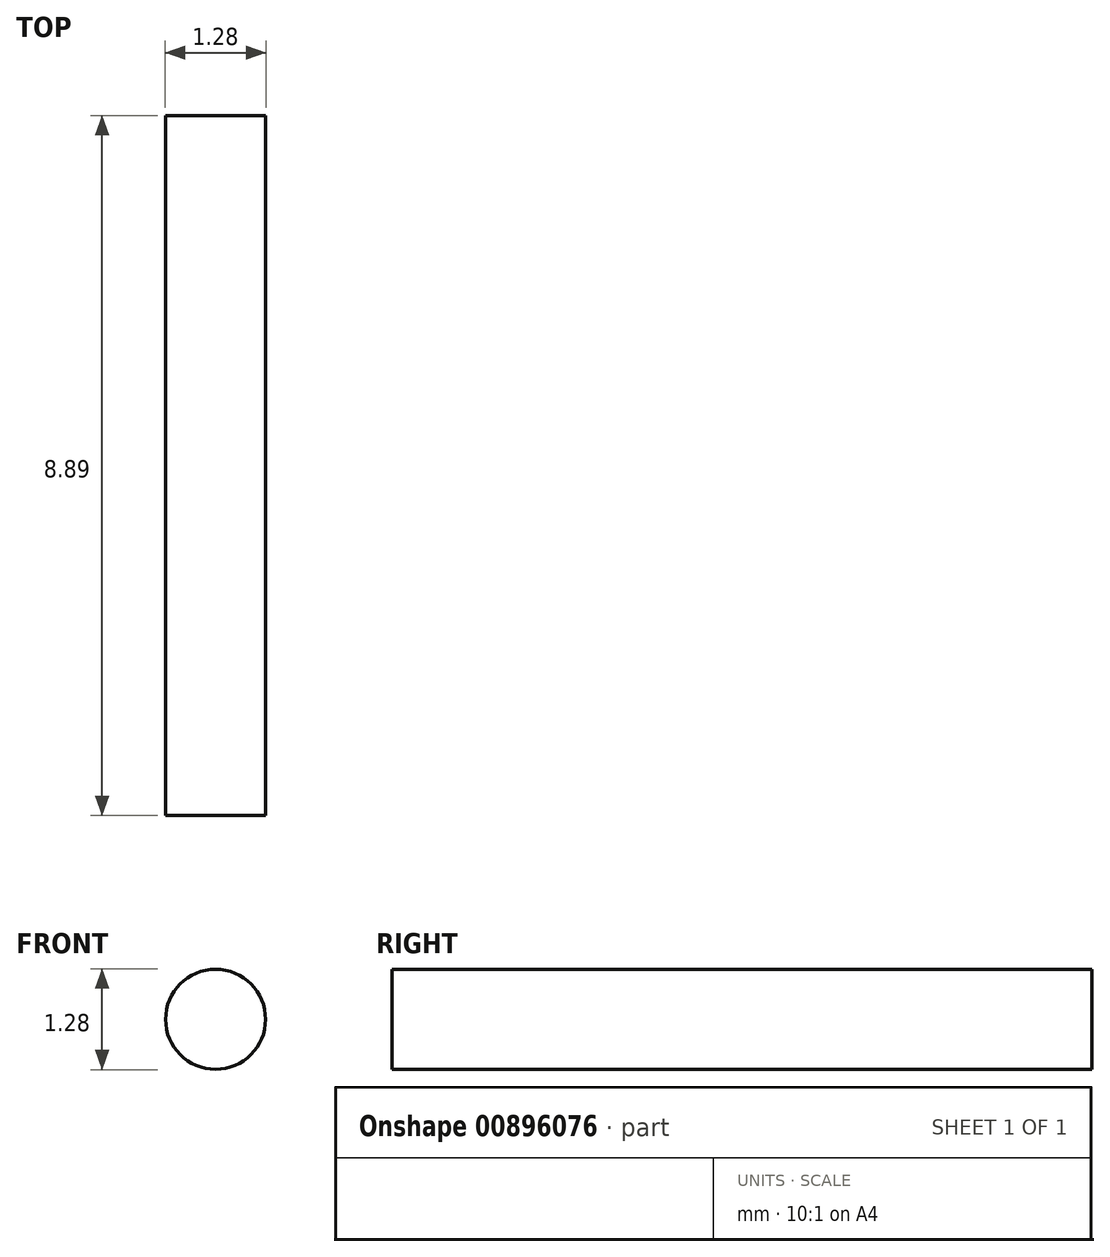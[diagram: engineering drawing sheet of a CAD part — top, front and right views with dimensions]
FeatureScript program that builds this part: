
annotation { "Feature Type Name" : "Feature", "Feature Type Description" : "" }
export const myFeature = defineFeature(function(context is Context, id is Id, definition is map)
    precondition{}
    {
        {
            var Q0;
            Q0=qCreatedBy(makeId("Front.planeOp"),FACE);
            var sketch = newSketch(context, id + "F0", { "sketchPlane" : qUnion([Q0])});
            skCircle(sketch, "E0", {"center": v(0, 0) * mm, "radius": 0.64 * mm});
            skSolve(sketch);
        }
        {
            var Q0;
            Q0=makeQuery(id+"F0.imprint","IMPRINT",FACE,{"disambiguationData":[TD([[makeQuery(id+"F0.imprint","IMPRINT",EDGE,{"derivedFrom":sQuery(id+"F0.wireOp",EDGE,"E0")}),1.0]])]});
            extrude(context, id + "F1", {"entities" : qUnion([Q0]), "depth" : 8.9 * mm, "offsetDistance" : 25.4 * mm});
        }
    });
